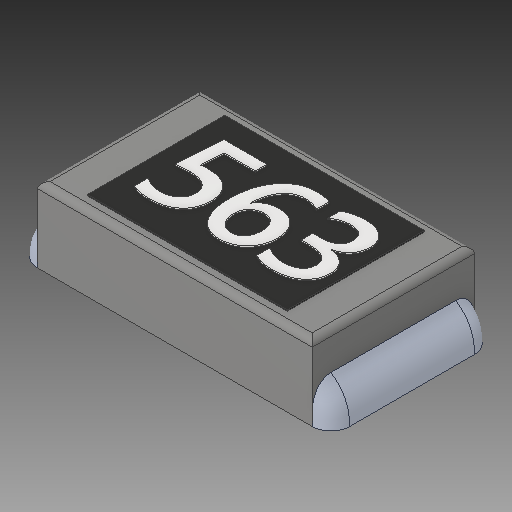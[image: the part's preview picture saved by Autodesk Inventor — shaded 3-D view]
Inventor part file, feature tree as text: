
AUTODESK INVENTOR PART (.ipt)
format: ipt  version: 2018.3 (Build 223284000, 284)  size: 306,688 bytes
history: native  units: mm
features: other x4, fillet x1, mirror x1
ambient origin geometry x8: Origin, YZ Plane, XZ Plane, XY Plane, X Axis, Y Axis, Z Axis, Center Point
bodies: Body1 (feature_tree), Body2 (feature_tree), Body3 (feature_tree)
feature tree (6):
  other  "Sólido1"
  other  "Sólido2"
  other  "Sólido3"
  fillet  "Fillet2"  [1 undecoded]
  mirror  "Mirror1"
  other  "Boss-Extrude4"
note: 1 required parameter value undecoded (feature->parameter linkage not recoverable at this tier; creation-order binding heuristic only, values carry confidence <= 0.55)
